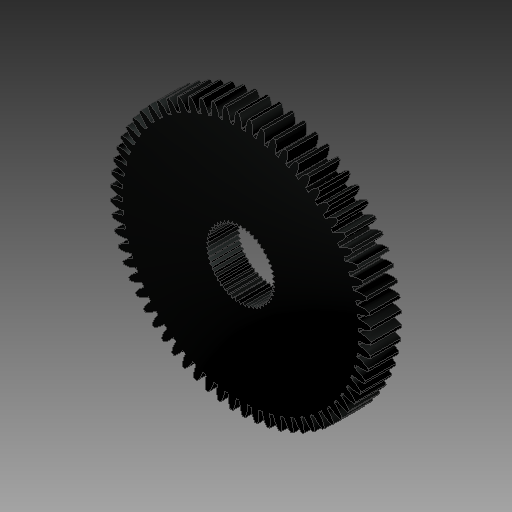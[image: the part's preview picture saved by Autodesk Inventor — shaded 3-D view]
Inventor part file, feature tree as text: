
AUTODESK INVENTOR PART (.ipt)
format: ipt  version: 2018 (Build 220112000, 112)  size: 1,057,792 bytes
history: native  units: in
note: dims shown in document units (in); Inventor stores cm internally (conversion verified against a paired STEP export)
features: sketch x6, extrude x5, pattern_circular x2, plane x1
ambient origin geometry x8: Origin, YZ Plane, XZ Plane, XY Plane, X Axis, Y Axis, Z Axis, Center Point
bodies: Solid1 (feature_tree)
feature tree (14):
  sketch  "Sketch2"  dims[d0=1.2992in d1=0.1374in]
  extrude  "Extrusion1"  Depth=0.1374in
  extrude  "Extrusion3"  Depth=0.0591in
  pattern_circular  "Circular Pattern1"  [2 undecoded]
  extrude  "Extrusion12"  Depth=0.3937in TaperAngle=360.0deg
  extrude  "Extrusion19"  Depth=0.3937in
  extrude  "Extrusion21"  Depth=0.3937in
  pattern_circular  "Circular Pattern3"  [2 undecoded]
  plane  "Work Plane17"
  sketch  "Sketch4"  dims[d6=0.2222in d7=0.0591in]
  sketch  "Sketch5"  dims[d8=0.1631in]
  sketch  "Sketch24"  dims[d9=0.0094in]
  sketch  "Sketch47"  dims[d10=1.4567in]
  sketch  "Sketch49"  dims[d12=0.1575in d13=0.0in d16=0.1969in d17=0.0in d18=25.9843in d19=360.0deg d61=0.0787in d62=0.3009in d64=0.0039in d121=1.3386in d122=2.6772in d123=0.3937in d124=0.0in d183=0.3268in d184=0.3937in d185=0.0in d193=0.0247in d195=0.3268in d196=0.1752in d197=0.3937in d198=0.0in d199=19.685in d200=360.0deg d202=-0.0787in]
note: 4 required parameter values undecoded (feature->parameter linkage not recoverable at this tier; creation-order binding heuristic only, values carry confidence <= 0.55)
